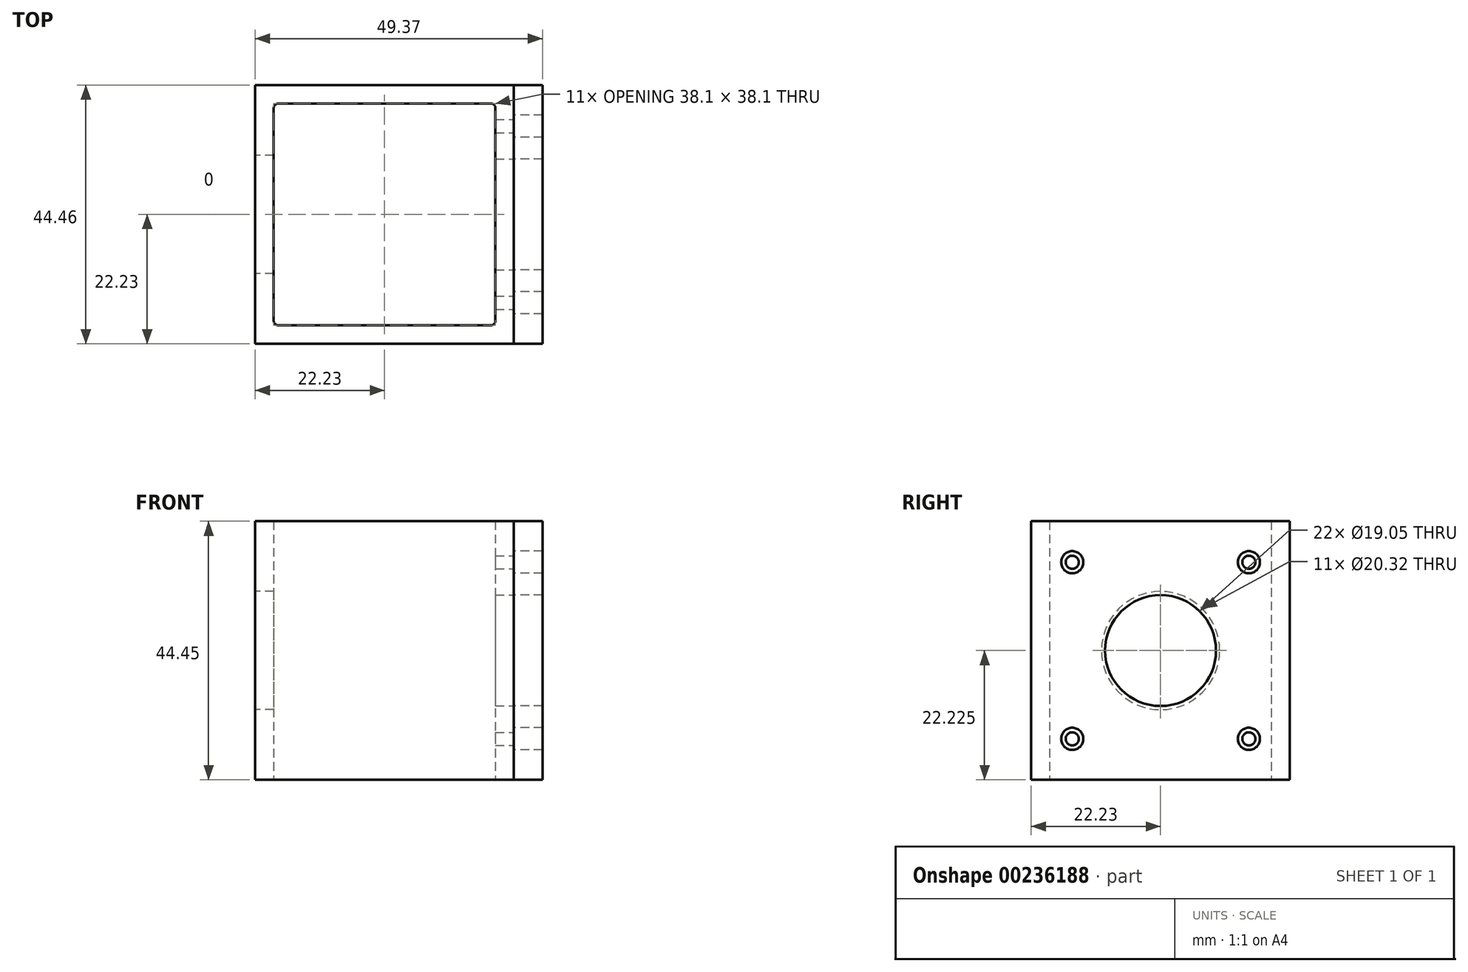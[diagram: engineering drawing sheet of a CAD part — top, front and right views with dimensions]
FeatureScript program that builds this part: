
annotation { "Feature Type Name" : "Feature", "Feature Type Description" : "" }
export const myFeature = defineFeature(function(context is Context, id is Id, definition is map)
    precondition{}
    {
        {
            var Q0;
            Q0=qCreatedBy(makeId("Top.planeOp"),FACE);
            var sketch = newSketch(context, id + "F0", { "sketchPlane" : qUnion([Q0])});
            skLineSegment(sketch, "E0.bottom", {"start": v(22.23, -22.23) * mm, "end": v(-22.23, -22.23) * mm});
            skLineSegment(sketch, "E0.top", {"start": v(22.23, 22.23) * mm, "end": v(-22.22, 22.22) * mm});
            skLineSegment(sketch, "E0.left", {"start": v(22.23, -22.23) * mm, "end": v(22.23, 22.23) * mm});
            skLineSegment(sketch, "E0.right", {"start": v(-22.23, -22.23) * mm, "end": v(-22.22, 22.23) * mm});
            skPoint(sketch, "E0.middle", {"position": v(0, 0) * mm});
            skLineSegment(sketch, "E1.bottom", {"start": v(18.29, -19.05) * mm, "end": v(-18.29, -19.05) * mm});
            skLineSegment(sketch, "E1.top", {"start": v(18.29, 19.05) * mm, "end": v(-18.29, 19.05) * mm});
            skLineSegment(sketch, "E1.left", {"start": v(19.05, -18.29) * mm, "end": v(19.05, 18.29) * mm});
            skLineSegment(sketch, "E1.right", {"start": v(-19.05, -18.29) * mm, "end": v(-19.05, 18.29) * mm});
            skPoint(sketch, "E2.visualSharp", {"position": v(-19.05, 19.05) * mm});
            skArc(sketch, "E2.filletArc", {"start": v(-18.29, 19.05) * mm, "mid": v(-18.83, 18.83) * mm, "end": v(-19.05, 18.29) * mm});
            skPoint(sketch, "E3.visualSharp", {"position": v(19.05, 19.05) * mm});
            skArc(sketch, "E3.filletArc", {"start": v(19.05, 18.29) * mm, "mid": v(18.83, 18.83) * mm, "end": v(18.29, 19.05) * mm});
            skPoint(sketch, "E4.visualSharp", {"position": v(19.05, -19.05) * mm});
            skArc(sketch, "E4.filletArc", {"start": v(18.29, -19.05) * mm, "mid": v(18.83, -18.83) * mm, "end": v(19.05, -18.29) * mm});
            skPoint(sketch, "E5.visualSharp", {"position": v(-19.05, -19.05) * mm});
            skArc(sketch, "E5.filletArc", {"start": v(-19.05, -18.29) * mm, "mid": v(-18.83, -18.83) * mm, "end": v(-18.29, -19.05) * mm});
            skSolve(sketch);
        }
        {
            var Q0;
            Q0 = qSketchRegion(id + "F0", true);
            extrude(context, id + "F1", {"entities" : qUnion([Q0]), "depth" : 44.45 * mm});
        }
        {
            var Q0;
            Q0=makeQuery(id+"F1.opExtrude","SWEPT_FACE",FACE,{"disambiguationData":[OSD([sQuery(id+"F0.wireOp",EDGE,"E0.left")])]});
            var sketch = newSketch(context, id + "F2", { "sketchPlane" : qUnion([Q0])});
            skLineSegment(sketch, "E6", {"start": v(-22.23, 22.23) * mm, "end": v(0, 22.23) * mm});
            skLineSegment(sketch, "E7.bottom", {"start": v(15.18, 7.05) * mm, "end": v(-15.18, 7.05) * mm});
            skLineSegment(sketch, "E7.top", {"start": v(15.18, 37.4) * mm, "end": v(-15.18, 37.4) * mm});
            skLineSegment(sketch, "E7.left", {"start": v(15.18, 7.05) * mm, "end": v(15.18, 37.4) * mm});
            skLineSegment(sketch, "E7.right", {"start": v(-15.18, 7.05) * mm, "end": v(-15.18, 37.4) * mm});
            skPoint(sketch, "E7.middle", {"position": v(0, 22.23) * mm});
            skSolve(sketch);
        }
        {
            var Q0;
            Q0=sQuery(id+"F2.wireOp",VERTEX,"E7.bottom.end");
            var Q1;
            Q1=sQuery(id+"F2.wireOp",VERTEX,"E7.top.end");
            var Q2;
            Q2=sQuery(id+"F2.wireOp",VERTEX,"E7.top.start");
            var Q3;
            Q3=sQuery(id+"F2.wireOp",VERTEX,"E7.left.start");
            var Q4;
            Q4=makeQuery(id+"F1.opExtrude","SWEPT_BODY",BODY,{"disambiguationData":[OSD([sQuery(id+"F0.wireOp",EDGE,"E0.bottom"),sQuery(id+"F0.wireOp",EDGE,"E0.top"),sQuery(id+"F0.wireOp",EDGE,"E0.left"),sQuery(id+"F0.wireOp",EDGE,"E0.right"),sQuery(id+"F0.wireOp",EDGE,"E1.bottom"),sQuery(id+"F0.wireOp",EDGE,"E1.top"),sQuery(id+"F0.wireOp",EDGE,"E1.left"),sQuery(id+"F0.wireOp",EDGE,"E1.right"),sQuery(id+"F0.wireOp",EDGE,"E2.filletArc"),sQuery(id+"F0.wireOp",EDGE,"E3.filletArc"),sQuery(id+"F0.wireOp",EDGE,"E4.filletArc"),sQuery(id+"F0.wireOp",EDGE,"E5.filletArc")])]});
            hole(context, id + "F3", {"style" : HoleStyle.SIMPLE, "endStyle" : HoleEndStyle.BLIND, "standardTappedOrClearance" : lookupTablePath({ "standard" : "ANSI", "engagement" : "75%", "pitch" : "40 tpi", "size" : "#4", "type" : "Tapped" }), "standardBlindInLast" : lookupTablePath({ "standard" : "ANSI", "engagement" : "75%", "pitch" : "40 tpi", "size" : "#4", "type" : "Tapped" }), "holeDiameter" : 2.26 * mm, "holeDepth" : 12.7 * mm, "locations" : qUnion([Q0, Q1, Q2, Q3]), "scope" : qUnion([Q4]), "majorDiameter" : 2.84 * mm});
        }
        {
            var Q0;
            Q0=makeQuery(id+"F1.opExtrude","SWEPT_FACE",FACE,{"disambiguationData":[OSD([sQuery(id+"F0.wireOp",EDGE,"E0.left")])]});
            var sketch = newSketch(context, id + "F4", { "sketchPlane" : qUnion([Q0])});
            skCircle(sketch, "E8", {"center": v(0, 22.23) * mm, "radius": 9.53 * mm});
            skSolve(sketch);
        }
        {
            var Q0;
            Q0 = qSketchRegion(id + "F4", true);
            extrude(context, id + "F5", {"entities" : qUnion([Q0]), "operationType" : NewBodyOperationType.REMOVE, "oppositeDirection" : true, "depth" : 25.4 * mm});
        }
        {
            var Q0;
            Q0=makeQuery(id+"F1.opExtrude","SWEPT_FACE",FACE,{"disambiguationData":[OSD([sQuery(id+"F0.wireOp",EDGE,"E0.right")])]});
            var sketch = newSketch(context, id + "F6", { "sketchPlane" : qUnion([Q0])});
            skCircle(sketch, "E9", {"center": v(0, 22.23) * mm, "radius": 10.16 * mm});
            skSolve(sketch);
        }
        {
            var Q0;
            Q0 = qSketchRegion(id + "F6", true);
            extrude(context, id + "F7", {"entities" : qUnion([Q0]), "operationType" : NewBodyOperationType.REMOVE, "oppositeDirection" : true, "depth" : 25.4 * mm});
        }
        {
            var Q0;
            Q0=makeQuery(id+"F1.opExtrude","SWEPT_FACE",FACE,{"disambiguationData":[OSD([sQuery(id+"F0.wireOp",EDGE,"E0.left")])]});
            var sketch = newSketch(context, id + "F8", { "sketchPlane" : qUnion([Q0])});
            skCircle(sketch, "E10", {"center": v(0, 22.23) * mm, "radius": 9.53 * mm});
            skLineSegment(sketch, "E11", {"start": v(0, 22.23) * mm, "end": v(-15.18, 37.4) * mm});
            skLineSegment(sketch, "E12.1.0", {"start": v(0, 22.23) * mm, "end": v(-15.18, 7.05) * mm});
            skLineSegment(sketch, "E12.2.0", {"start": v(0, 22.23) * mm, "end": v(15.18, 7.05) * mm});
            skLineSegment(sketch, "E12.3.0", {"start": v(0, 22.23) * mm, "end": v(15.18, 37.4) * mm});
            skLineSegment(sketch, "E13.bottom", {"start": v(22.23, 0) * mm, "end": v(-22.23, 0) * mm});
            skLineSegment(sketch, "E13.top", {"start": v(22.23, 44.45) * mm, "end": v(-22.23, 44.45) * mm});
            skLineSegment(sketch, "E13.left", {"start": v(22.22, 0) * mm, "end": v(22.23, 44.45) * mm});
            skLineSegment(sketch, "E13.right", {"start": v(-22.23, 0) * mm, "end": v(-22.23, 44.45) * mm});
            skCircle(sketch, "E14", {"center": v(-15.18, 37.4) * mm, "radius": 1.9 * mm});
            skCircle(sketch, "E15.1.0", {"center": v(-15.18, 7.05) * mm, "radius": 1.9 * mm});
            skCircle(sketch, "E15.2.0", {"center": v(15.18, 7.05) * mm, "radius": 1.9 * mm});
            skCircle(sketch, "E15.3.0", {"center": v(15.18, 37.4) * mm, "radius": 1.9 * mm});
            skSolve(sketch);
        }
        {
            var Q0;
            Q0=makeQuery(id+"F8.imprint","IMPRINT",FACE,{"disambiguationData":[TD([[makeQuery(id+"F8.imprint","IMPRINT",EDGE,{"derivedFrom":sQuery(id+"F8.wireOp",EDGE,"E13.bottom")}),1.0]])]});
            extrude(context, id + "F9", {"entities" : qUnion([Q0]), "depth" : 4.9 * mm});
        }
    });
